# Revit family: 26356 Стационарное зарядное устройство и точка доступа Wi-Fi «Валли» на стойке Хоббика
name_source: partatom
category: Антураж
revit_build: Autodesk Revit 2018 (Build: 20180423_1000(x64)
units: mm (PartAtom-declared; Revit-internal decimal feet)

## family parameters
Всегда вертикально = Да
Источник визуального образа = Геометрия семейства
На основе рабочей плоскости = Нет
Общий = Нет
При загрузке вырезать с полостями = Нет
Точка расчета площади = Нет

## types (7) — shared parameters
URL = https://hobbyka.ru
Артикул товара = Арт. 26356
Высота = 472 мм
Группа модели = Умная городская мебель
Длина = 180 мм
Изготовитель = ООО «Хоббика»
Изображение типоразмера = Стационарное зарядное устройство и точка доступа Wi-Fi «Валли» на стойке Арт 26356.jpg
Материал изделия = Сталь
Цвет каркаса = Серый
Цвет отделки = Оранжевый
Ширина = 160 мм

## per-type parameters (varying)
| type | 1 розетка USB 3А, 1 розетка Type-C 3А, 1 розетка 220В | 2 розетки 220В | 2 розетки Type-C 3А и 1 розетка 220В | 2 розетки USB 3А и 1 розетка 220В | 2 розетки USB 3А и 2 розетки Type-C 3А | 4 розетки Type-C 3А | 4 розетки USB 3А | Описание |
| 1 розетка USB 3А, 1 розетка Type-C 3А, 1 розетка 220В | Да | Нет | Нет | Нет | Нет | Нет | Нет | Стационарное зарядное устройство и точка доступа Wi-Fi «Валли» на стойке. Версия 1 розетка USB 3А, 1 розетка Type-C 3А, 1 розетка 220В |
| 2 розетки 220В | Нет | Да | Нет | Нет | Нет | Нет | Нет | Стационарное зарядное устройство и точка доступа Wi-Fi «Валли» на стойке. Версия 2 розетки 220В |
| 2 розетки Type-C 3А и 1 розетка 220В | Нет | Нет | Да | Нет | Нет | Нет | Нет | Стационарное зарядное устройство и точка доступа Wi-Fi «Валли» на стойке. Версия 2 розетки Type-C 3А, 1 розетка 220В |
| 2 розетки USB 3А и 1 розетка 220В | Нет | Нет | Нет | Да | Нет | Нет | Нет | Стационарное зарядное устройство и точка доступа Wi-Fi «Валли» на стойке. Версия 2 розетки USB 3А, 1 розетка 220В |
| 2 розетки USB 3А и 2 розетки Type-C 3А | Нет | Нет | Нет | Нет | Да | Нет | Нет | Стационарное зарядное устройство и точка доступа Wi-Fi «Валли» на стойке. Версия 2 розетки USB 3А, 2 розетки Type-C 3А |
| 4 розетки Type-C 3А | Нет | Нет | Нет | Нет | Нет | Да | Нет | Стационарное зарядное устройство и точка доступа Wi-Fi «Валли» на стойке. Версия 4 розетки Type-C 3А |
| 4 розетки USB 3А | Нет | Нет | Нет | Нет | Нет | Нет | Да | Стационарное зарядное устройство и точка доступа Wi-Fi «Валли» на стойке. Версия 2 розетки USB 3А |
